# Revit family: BLU-125, BLU Magnetic damper
name_source: partatom
category: Duct Accessories
revit_build: Autodesk Revit 2018 (Build: 20170223_1515(x64)
units: mm (PartAtom-declared; Revit-internal decimal feet)

## family parameters
Always vertical = Yes
Cut with Voids When Loaded = No
OmniClass Number = 23.75.70.11.14.14
OmniClass Title = Dampers for Air Ductwork
Part Type = Damper
Round Connector Dimension = Use Diameter
Shared = No
Work Plane-Based = No

## types (2) — shared parameters
Colour. = blue
Damper Length = 150 mm
Damper Material = <By Category>
Half Damper Length = 75 mm
Material. = plastic
anglXY1 = 180.00°
anglXY2 = 0.00°
anglZ1 = 0.00°
anglZ2 = 0.00°
lengXY1 = 600 mm
lengXY2 = 600 mm
lengXYZ1 = 500 mm  [stored 1.64042 ft]
lengXYZ2 = 500 mm  [stored 1.64042 ft]
zero-valued in all types: lengX1, lengY1, lengY2, lengZ1, lengZ2

## per-type parameters (varying)
| type | Diameter (D). | Length (A). | Length (B). | Type. | diamcon1 | diamcon2 | lengX2 |
| BLU.160, Diameter D=160, length A=20, length B=110 | 160 | 20 | 110 | BLU.160 | 160 mm | 160 mm | 20 mm  [stored 0.0656168 ft] |
| BLU.125, Diameter D=125, length A=18, length B=90 | 125 | 18 | 90 | BLU.125 | 125 mm | 125 mm | 18 mm  [stored 0.0590551 ft] |

note: column(s) folded — value = type name in every type: Geometry

note: [stored X ft] marks values corroborated as IEEE doubles in the binary element streams (Revit-internal decimal feet)

## geometry (parser evidence)
native form markers: Sweep x7
no freeform markers — native parametric forms only
